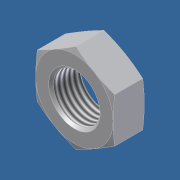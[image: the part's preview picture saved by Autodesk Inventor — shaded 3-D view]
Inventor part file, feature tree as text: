
AUTODESK INVENTOR PART (.ipt)
format: ipt  version: 2012 (Build 160160000, 160)  size: 129,536 bytes
history: native  units: in
note: dims shown in document units (in); Inventor stores cm internally (conversion verified against a paired STEP export)
features: other x70, sketch x3, revolve x2, extrude x1, thread x1
ambient origin geometry x8: Origin, YZ Plane, XZ Plane, XY Plane, X Axis, Y Axis, Z Axis, Center Point
bodies: Solid1 (feature_tree)
feature tree (77):
  sketch  "Sketch_8"  dims[d0=360.0deg d1=0.38in d2=0.0in]
  sketch  "Sketch_10"  dims[d3=360.0deg d4=0.38in d5=0.0in]
  revolve  "Revolution1"  [1 undecoded]
  extrude  "Extrusion1"  Depth=0.38in TaperAngle=0.0deg
  revolve  "Revolution2"  [1 undecoded]
  thread  "Thread1"  [1 undecoded]
  other  "NUT_XY"
  other  "NUT_YZ"
  other  "NUT_ZX"
  other  "NUT_X"
  other  "NUT_Y"
  other  "NUT_Z"
  other  "NUT_Center"
  other  "a1_XY"
  other  "a1_YZ"
  other  "a1_ZX"
  other  "a1_X"
  other  "a1_Y"
  other  "a1_Z"
  other  "a1_Center"
  other  "a2_XY"
  other  "a2_YZ"
  other  "a2_ZX"
  other  "a2_X"
  other  "a2_Y"
  other  "a2_Z"
  other  "a2_Center"
  other  "b1_XY"
  other  "b1_YZ"
  other  "b1_ZX"
  other  "b1_X"
  other  "b1_Y"
  other  "b1_Z"
  other  "b1_Center"
  other  "b2_XY"
  other  "b2_YZ"
  other  "b2_ZX"
  other  "b2_X"
  other  "b2_Y"
  other  "b2_Z"
  other  "b2_Center"
  other  "e_XY"
  other  "e_YZ"
  other  "e_ZX"
  other  "e_X"
  other  "e_Y"
  other  "e_Z"
  other  "e_Center"
  other  "th1_XY"
  other  "th1_YZ"
  other  "th1_ZX"
  other  "th1_X"
  other  "th1_Y"
  other  "th1_Z"
  other  "th1_Center"
  other  "th2_XY"
  other  "th2_YZ"
  other  "th2_ZX"
  other  "th2_X"
  other  "th2_Y"
  other  "th2_Z"
  other  "th2_Center"
  other  "ol1_XY"
  other  "ol1_YZ"
  other  "ol1_ZX"
  other  "ol1_X"
  other  "ol1_Y"
  other  "ol1_Z"
  other  "ol1_Center"
  other  "ol2_XY"
  other  "ol2_YZ"
  other  "ol2_ZX"
  other  "ol2_X"
  other  "ol2_Y"
  other  "ol2_Z"
  other  "ol2_Center"
  sketch  "Sketch_11"
note: 3 required parameter values undecoded (feature->parameter linkage not recoverable at this tier; creation-order binding heuristic only, values carry confidence <= 0.55)